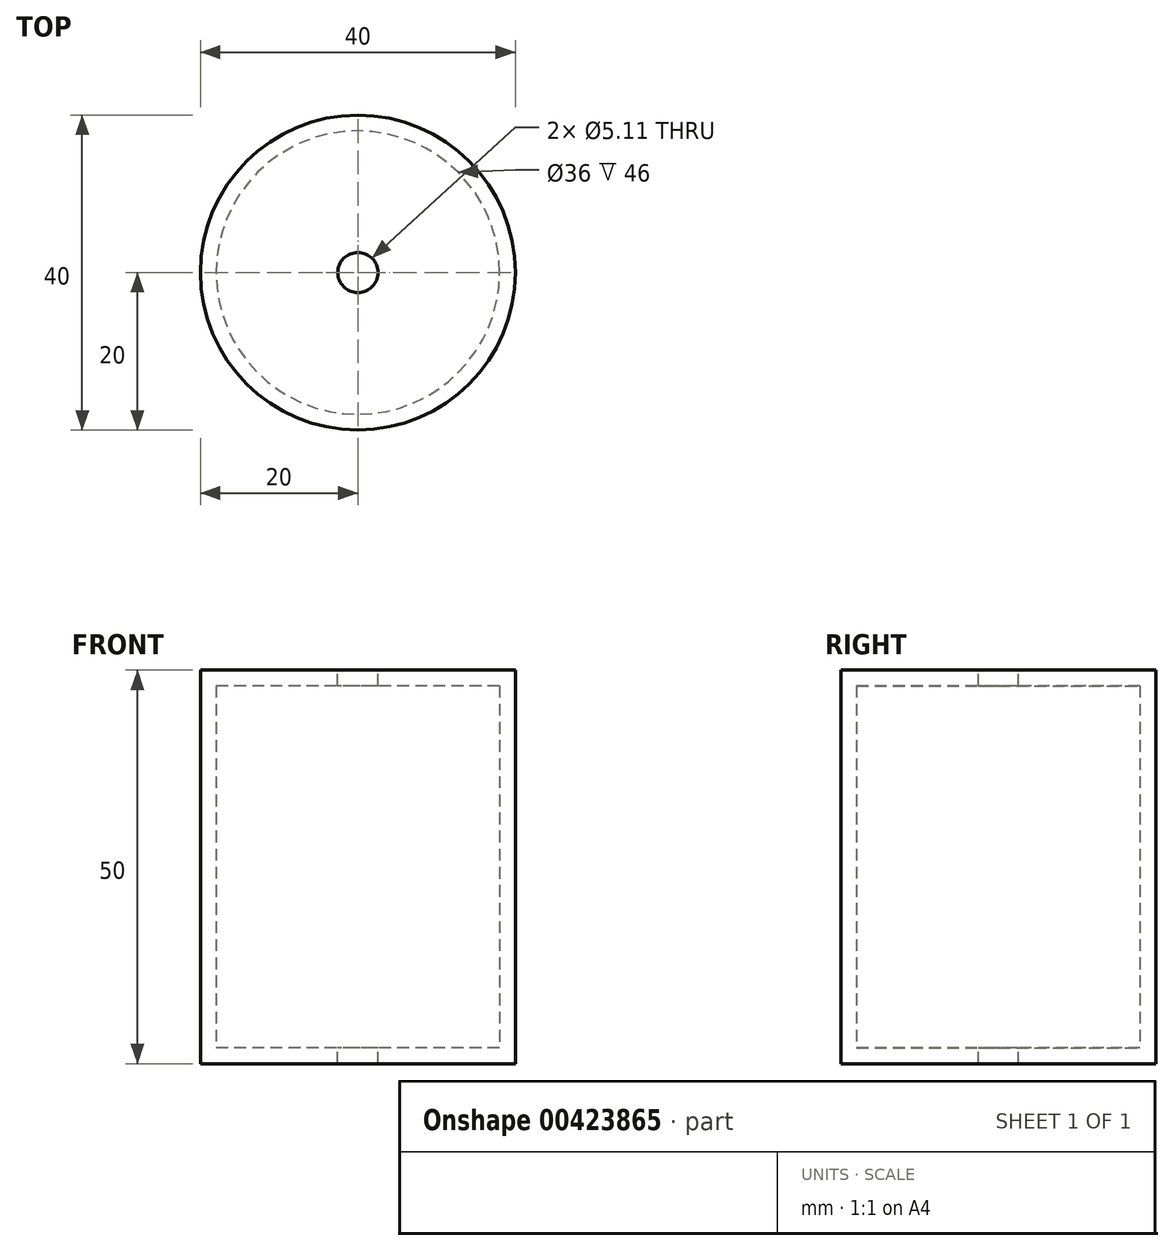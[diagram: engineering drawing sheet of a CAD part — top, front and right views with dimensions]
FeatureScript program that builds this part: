
annotation { "Feature Type Name" : "Feature", "Feature Type Description" : "" }
export const myFeature = defineFeature(function(context is Context, id is Id, definition is map)
    precondition{}
    {
        {
            var Q0;
            Q0=qCreatedBy(makeId("Front.planeOp"),FACE);
            var sketch = newSketch(context, id + "F0", { "sketchPlane" : qUnion([Q0])});
            skLineSegment(sketch, "E0.bottom", {"start": v(-10, -25) * mm, "end": v(10, -25) * mm});
            skLineSegment(sketch, "E0.top", {"start": v(-10, 25) * mm, "end": v(10, 25) * mm});
            skLineSegment(sketch, "E0.left", {"start": v(-10, -25) * mm, "end": v(-10, 25) * mm});
            skLineSegment(sketch, "E0.right", {"start": v(10, -25) * mm, "end": v(10, 25) * mm});
            skPoint(sketch, "E0.middle", {"position": v(0, 0) * mm});
            skSolve(sketch);
        }
        {
            var Q0;
            Q0=makeQuery(id+"F0.imprint","IMPRINT",FACE,{"disambiguationData":[TD([[makeQuery(id+"F0.imprint","IMPRINT",EDGE,{"derivedFrom":sQuery(id+"F0.wireOp",EDGE,"E0.bottom")}),1.0]])]});
            var Q1;
            Q1=sQuery(id+"F0.wireOp",EDGE,"E0.right");
            revolve(context, id + "F1", {"entities" : qUnion([Q0]), "axis" : qUnion([Q1]), "revolveType" : RevolveType.FULL});
        }
        {
            var Q0;
            Q0=makeQuery(id+"F1.opRevolve","SWEPT_FACE",FACE,{"disambiguationData":[OSD([sQuery(id+"F0.wireOp",EDGE,"E0.left")])]});
            var Q1;
            Q1=makeQuery(id+"F1.opRevolve","SWEPT_BODY",BODY,{"disambiguationData":[OSD([sQuery(id+"F0.wireOp",EDGE,"E0.bottom"),sQuery(id+"F0.wireOp",EDGE,"E0.top"),sQuery(id+"F0.wireOp",EDGE,"E0.left"),sQuery(id+"F0.wireOp",EDGE,"E0.right")])]});
            shell(context, id + "F2", {"isHollow" : true, "entities" : qUnion([Q0]), "parts" : qUnion([Q1]), "thickness" : 2 * mm});
        }
        {
            var Q0;
            Q0=makeQuery(id+"F1.opRevolve","SWEPT_FACE",FACE,{"disambiguationData":[OSD([sQuery(id+"F0.wireOp",EDGE,"E0.top")])]});
            var sketch = newSketch(context, id + "F3", { "sketchPlane" : qUnion([Q0])});
            skPoint(sketch, "E1", {"position": v(10, 0) * mm});
            skSolve(sketch);
        }
        {
            var Q0;
            Q0=sQuery(id+"F3.wireOp",VERTEX,"E1");
            var Q1;
            Q1=makeQuery(id+"F1.opRevolve","SWEPT_BODY",BODY,{"disambiguationData":[OSD([sQuery(id+"F0.wireOp",EDGE,"E0.bottom"),sQuery(id+"F0.wireOp",EDGE,"E0.top"),sQuery(id+"F0.wireOp",EDGE,"E0.left"),sQuery(id+"F0.wireOp",EDGE,"E0.right")])]});
            hole(context, id + "F4", {"style" : HoleStyle.SIMPLE, "endStyle" : HoleEndStyle.THROUGH, "standardTappedOrClearance" : lookupTablePath({ "standard" : "ANSI", "engagement" : "75%", "pitch" : "20 tpi", "size" : "1/4", "type" : "Tapped" }), "standardBlindInLast" : lookupTablePath({ "standard" : "ANSI", "engagement" : "75%", "pitch" : "20 tpi", "size" : "1/4", "type" : "Tapped" }), "holeDiameter" : 5.1 * mm, "showTappedDepth" : true, "isTappedThrough" : true, "tappedDepth" : 12 * mm, "tapClearance" : 3, "locations" : qUnion([Q0]), "scope" : qUnion([Q1]), "majorDiameter" : 6.35 * mm});
        }
    });
